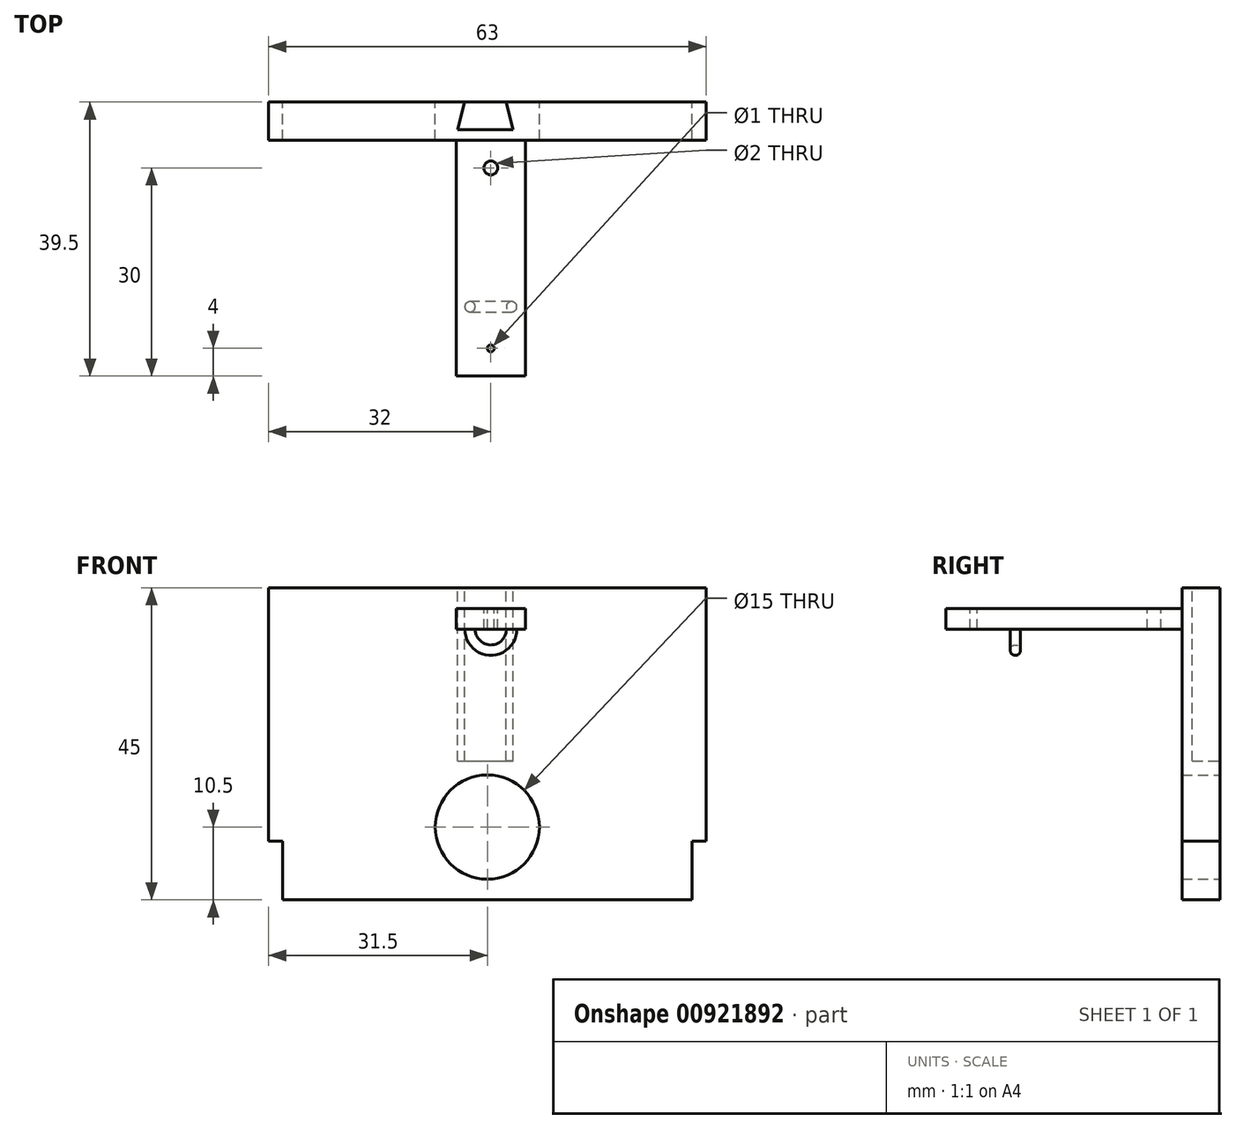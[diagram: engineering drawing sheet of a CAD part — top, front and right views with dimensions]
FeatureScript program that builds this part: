
annotation { "Feature Type Name" : "Feature", "Feature Type Description" : "" }
export const myFeature = defineFeature(function(context is Context, id is Id, definition is map)
    precondition{}
    {
        {
            var Q0;
            Q0=qCreatedBy(makeId("Front.planeOp"),FACE);
            var sketch = newSketch(context, id + "F0", { "sketchPlane" : qUnion([Q0])});
            skLineSegment(sketch, "E0", {"start": v(0, 0) * mm, "end": v(0, 8.5) * mm});
            skLineSegment(sketch, "E1", {"start": v(0, 8.5) * mm, "end": v(-2, 8.5) * mm});
            skLineSegment(sketch, "E2", {"start": v(-2, 8.5) * mm, "end": v(-2, 45) * mm});
            skLineSegment(sketch, "E3", {"start": v(-2, 45) * mm, "end": v(61, 45) * mm});
            skLineSegment(sketch, "E4", {"start": v(61, 45) * mm, "end": v(61, 8.5) * mm});
            skLineSegment(sketch, "E5", {"start": v(61, 8.5) * mm, "end": v(59, 8.5) * mm});
            skLineSegment(sketch, "E6", {"start": v(59, 8.5) * mm, "end": v(59, 0) * mm});
            skLineSegment(sketch, "E7", {"start": v(59, 0) * mm, "end": v(0, 0) * mm});
            skCircle(sketch, "E8", {"center": v(29.5, 10.5) * mm, "radius": 7.5 * mm});
            skSolve(sketch);
        }
        {
            var Q0;
            Q0=makeQuery(id+"F0.imprint","IMPRINT",FACE,{"disambiguationData":[TD([[makeQuery(id+"F0.imprint","IMPRINT",EDGE,{"derivedFrom":sQuery(id+"F0.wireOp",EDGE,"E0")}),-1.0]])]});
            extrude(context, id + "F1", {"entities" : qUnion([Q0]), "flatOperationType" : FlatOperationType.REMOVE, "depth" : 5.5 * mm, "offsetDistance" : 25 * mm, "domain" : OperationDomain.MODEL});
        }
        {
            var Q0;
            Q0=makeQuery(id+"F1.opExtrude","SWEPT_FACE",FACE,{"disambiguationData":[OSD([sQuery(id+"F0.wireOp",EDGE,"E3")])]});
            var sketch = newSketch(context, id + "F2", { "sketchPlane" : qUnion([Q0])});
            skLineSegment(sketch, "E9", {"start": v(25.2, 0) * mm, "end": v(25.2, -4) * mm});
            skLineSegment(sketch, "E10", {"start": v(25.2, -4) * mm, "end": v(33.2, -4) * mm});
            skLineSegment(sketch, "E11", {"start": v(33.2, -4) * mm, "end": v(33.2, 0) * mm});
            skLineSegment(sketch, "E12", {"start": v(25.2, -4) * mm, "end": v(26.2, 0) * mm});
            skLineSegment(sketch, "E13", {"start": v(26.2, 0) * mm, "end": v(25.2, 0) * mm});
            skLineSegment(sketch, "E14", {"start": v(33.2, -4) * mm, "end": v(32.2, 0) * mm});
            skLineSegment(sketch, "E15", {"start": v(32.2, 0) * mm, "end": v(33.2, 0) * mm});
            skSolve(sketch);
        }
        {
            var Q0;
            Q0=makeQuery(id+"F2.imprint","IMPRINT",FACE,{"disambiguationData":[TD([[makeQuery(id+"F2.imprint","IMPRINT",EDGE,{"derivedFrom":sQuery(id+"F2.wireOp",EDGE,"E10")}),1.0]])]});
            extrude(context, id + "F3", {"entities" : qUnion([Q0]), "operationType" : NewBodyOperationType.REMOVE, "oppositeDirection" : true, "depth" : 25 * mm, "offsetDistance" : 25 * mm});
        }
        {
            var Q0;
            Q0=makeQuery(id+"F1.opExtrude","CAP_FACE",FACE,{"disambiguationData":[OSD([sQuery(id+"F0.wireOp",EDGE,"E0"),sQuery(id+"F0.wireOp",EDGE,"E1"),sQuery(id+"F0.wireOp",EDGE,"E2"),sQuery(id+"F0.wireOp",EDGE,"E3"),sQuery(id+"F0.wireOp",EDGE,"E4"),sQuery(id+"F0.wireOp",EDGE,"E5"),sQuery(id+"F0.wireOp",EDGE,"E6"),sQuery(id+"F0.wireOp",EDGE,"E7"),sQuery(id+"F0.wireOp",EDGE,"E8")])],"isStart":false});
            var sketch = newSketch(context, id + "F4", { "sketchPlane" : qUnion([Q0])});
            skLineSegment(sketch, "E16.bottom", {"start": v(25, 39) * mm, "end": v(35, 39) * mm});
            skLineSegment(sketch, "E16.top", {"start": v(25, 42) * mm, "end": v(35, 42) * mm});
            skLineSegment(sketch, "E16.left", {"start": v(25, 39) * mm, "end": v(25, 42) * mm});
            skLineSegment(sketch, "E16.right", {"start": v(35, 39) * mm, "end": v(35, 42) * mm});
            skSolve(sketch);
        }
        {
            var Q0;
            Q0=makeQuery(id+"F4.imprint","IMPRINT",FACE,{"disambiguationData":[TD([[makeQuery(id+"F4.imprint","IMPRINT",EDGE,{"derivedFrom":sQuery(id+"F4.wireOp",EDGE,"E16.bottom")}),1.0]])]});
            extrude(context, id + "F5", {"entities" : qUnion([Q0]), "operationType" : NewBodyOperationType.ADD, "depth" : 34 * mm, "offsetDistance" : 25 * mm});
        }
        {
            var Q0;
            Q0=makeQuery(id+"F5.opExtrude","SWEPT_FACE",FACE,{"disambiguationData":[OSD([sQuery(id+"F4.wireOp",EDGE,"E16.top")])]});
            var sketch = newSketch(context, id + "F6", { "sketchPlane" : qUnion([Q0])});
            skCircle(sketch, "E17", {"center": v(30, -35.5) * mm, "radius": 0.5 * mm});
            skCircle(sketch, "E18", {"center": v(30, -9.5) * mm, "radius": 1 * mm});
            skSolve(sketch);
        }
        {
            var Q0;
            Q0=makeQuery(id+"F6.imprint","IMPRINT",FACE,{"disambiguationData":[TD([[makeQuery(id+"F6.imprint","IMPRINT",EDGE,{"derivedFrom":sQuery(id+"F6.wireOp",EDGE,"C4gO8aF1-BuqH-Km8P-dodQ-VLEarZ2HRbCW")}),1.0]])]});
            var Q1;
            Q1=makeQuery(id+"F6.imprint","IMPRINT",FACE,{"disambiguationData":[TD([[makeQuery(id+"F6.imprint","IMPRINT",EDGE,{"derivedFrom":sQuery(id+"F6.wireOp",EDGE,"FNUx81zv-3VYq-Qe7D-XVgs-UJnYaS4Lcysl")}),1.0]])]});
            var Q2;
            Q2=makeQuery(id+"F6.imprint","IMPRINT",FACE,{"disambiguationData":[TD([[makeQuery(id+"F6.imprint","IMPRINT",EDGE,{"derivedFrom":sQuery(id+"F6.wireOp",EDGE,"l56A5l9P-hIxk-VUpc-47yu-x1oVep4XwpqC")}),1.0]])]});
            var Q3;
            Q3=makeQuery(id+"F6.imprint","IMPRINT",FACE,{"disambiguationData":[TD([[makeQuery(id+"F6.imprint","IMPRINT",EDGE,{"derivedFrom":sQuery(id+"F6.wireOp",EDGE,"E17")}),1.0]])]});
            extrude(context, id + "F7", {"entities" : qUnion([Q0, Q1, Q2, Q3]), "operationType" : NewBodyOperationType.REMOVE, "oppositeDirection" : true, "depth" : 6 * mm, "offsetDistance" : 25 * mm});
        }
        {
            var Q0;
            Q0=makeQuery(id+"F6.imprint","IMPRINT",FACE,{"disambiguationData":[TD([[makeQuery(id+"F6.imprint","IMPRINT",EDGE,{"derivedFrom":sQuery(id+"F6.wireOp",EDGE,"E18")}),1.0]])]});
            extrude(context, id + "F8", {"entities" : qUnion([Q0]), "operationType" : NewBodyOperationType.REMOVE, "oppositeDirection" : true, "depth" : 25 * mm, "offsetDistance" : 25 * mm});
        }
        {
            var Q0;
            Q0=makeQuery(id+"F5.opExtrude","SWEPT_FACE",FACE,{"disambiguationData":[OSD([sQuery(id+"F4.wireOp",EDGE,"E16.bottom")])]});
            var sketch = newSketch(context, id + "F9", { "sketchPlane" : qUnion([Q0])});
            skLineSegment(sketch, "E19", {"start": v(30, 9.5) * mm, "end": v(30, 16.39) * mm});
            skCircle(sketch, "E20", {"center": v(33, 29.5) * mm, "radius": 0.75 * mm});
            skSolve(sketch);
        }
        {
            var Q0;
            Q0=makeQuery(id+"F9.imprint","IMPRINT",FACE,{"disambiguationData":[TD([[makeQuery(id+"F9.imprint","IMPRINT",EDGE,{"derivedFrom":sQuery(id+"F9.wireOp",EDGE,"E20")}),1.0]])]});
            var Q1;
            Q1=sQuery(id+"F9.wireOp",EDGE,"E19");
            revolve(context, id + "F10", {"operationType" : NewBodyOperationType.ADD, "surfaceOperationType" : NewSurfaceOperationType.NEW, "entities" : qUnion([Q0]), "axis" : qUnion([Q1]), "revolveType" : RevolveType.ONE_DIRECTION, "oppositeDirection" : true, "angle" : 180 * degree});
        }
    });
